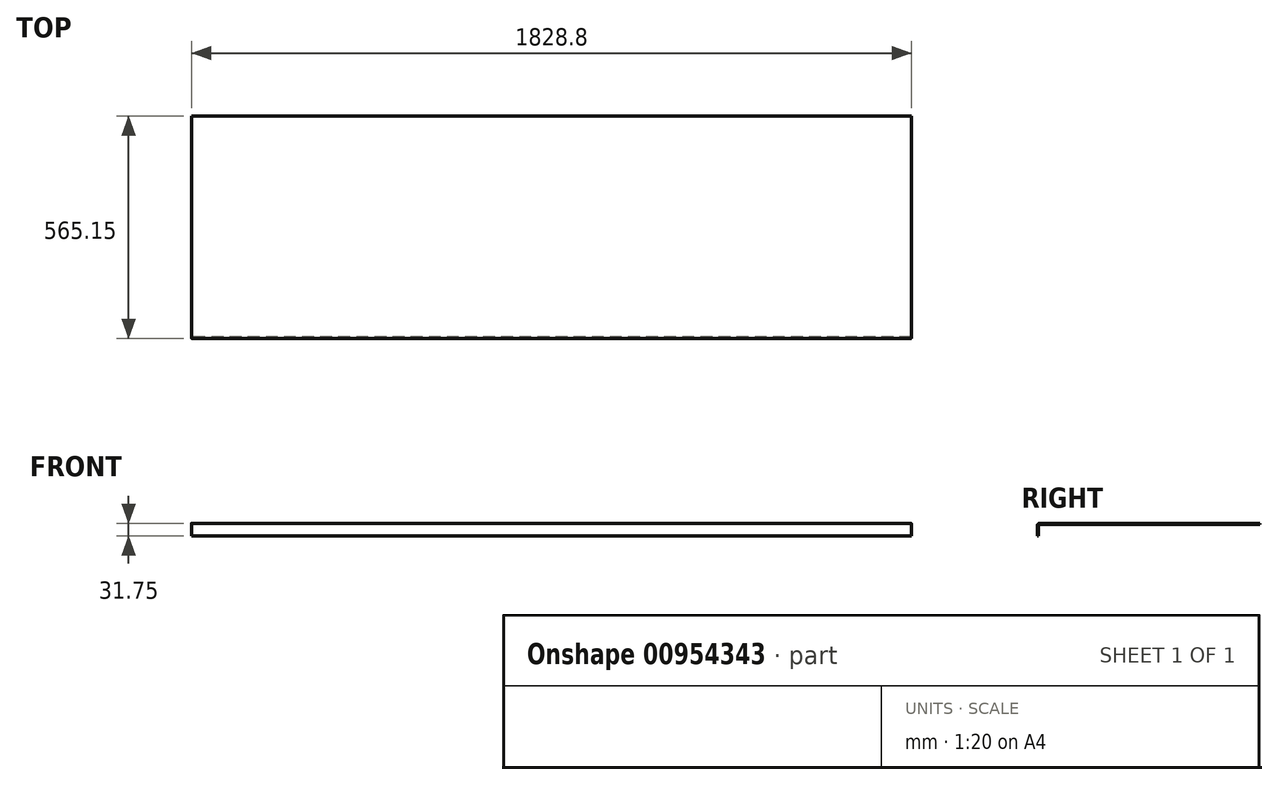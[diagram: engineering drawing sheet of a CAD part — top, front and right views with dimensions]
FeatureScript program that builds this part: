
annotation { "Feature Type Name" : "Feature", "Feature Type Description" : "" }
export const myFeature = defineFeature(function(context is Context, id is Id, definition is map)
    precondition{}
    {
        {
            var Q0;
            Q0=qCreatedBy(makeId("Right.planeOp"),FACE);
            var sketch = newSketch(context, id + "F0", { "sketchPlane" : qUnion([Q0])});
            skLineSegment(sketch, "E0.bottom", {"start": v(-306.3, -166.65) * mm, "end": v(255.67, -166.65) * mm});
            skLineSegment(sketch, "E0.top", {"start": v(-306.3, -169.83) * mm, "end": v(255.67, -169.83) * mm});
            skLineSegment(sketch, "E0.left", {"start": v(-306.3, -166.65) * mm, "end": v(-306.3, -169.83) * mm});
            skLineSegment(sketch, "E0.right", {"start": v(255.67, -166.65) * mm, "end": v(255.67, -169.83) * mm});
            skLineSegment(sketch, "E1.bottom", {"start": v(-306.3, -166.65) * mm, "end": v(-309.48, -166.65) * mm});
            skLineSegment(sketch, "E1.top", {"start": v(-306.3, -198.4) * mm, "end": v(-309.48, -198.4) * mm});
            skLineSegment(sketch, "E1.left", {"start": v(-306.3, -166.65) * mm, "end": v(-306.3, -198.4) * mm});
            skLineSegment(sketch, "E1.right", {"start": v(-309.48, -166.65) * mm, "end": v(-309.48, -198.4) * mm});
            skSolve(sketch);
        }
        {
            var Q0;
            {var subQ0=sQuery(id+"F0.wireOp",EDGE,"E0.bottom");Q0=makeQuery(id+"F0.imprint","IMPRINT",FACE,{"disambiguationData":[TD([[makeQuery(id+"F0.imprint","IMPRINT",EDGE,{"derivedFrom":subQ0}),-1.0]])]});}
            var Q1;
            {var subQ3=sQuery(id+"F0.wireOp",EDGE,"E1.bottom");Q1=makeQuery(id+"F0.imprint","IMPRINT",FACE,{"disambiguationData":[TD([[makeQuery(id+"F0.imprint","IMPRINT",EDGE,{"derivedFrom":subQ3}),1.0]])]});}
            extrude(context, id + "F1", {"entities" : qUnion([Q0, Q1]), "depth" : 1828.8 * mm, "offsetDistance" : 25.4 * mm, "symmetric" : true});
        }
        {
            var Q0;
            Q0=makeQuery(id+"F1.opExtrude","SWEPT_EDGE",EDGE,{"disambiguationData":[OSD([sQuery(id+"F0.wireOp",EDGE,"E1.bottom"),sQuery(id+"F0.wireOp",EDGE,"E1.right")])]});
            fillet(context, id + "F2", {"entities" : qUnion([Q0]), "radius" : 5.08 * mm, "tangentPropagation" : true, "allowEdgeOverflow" : false});
        }
    });
